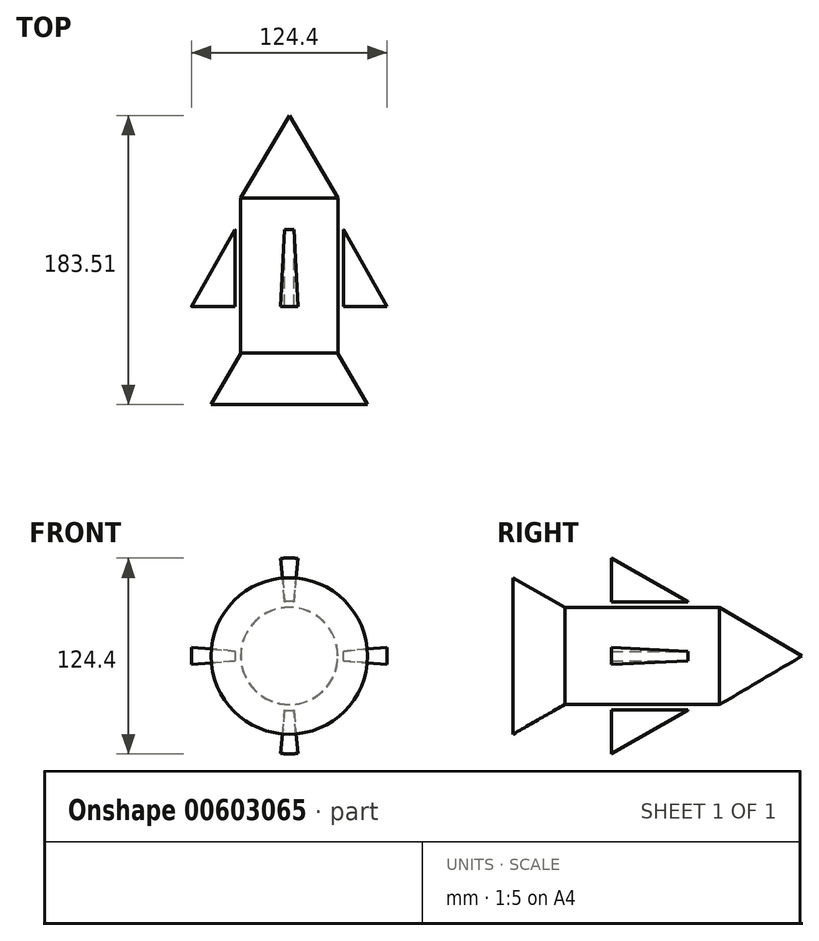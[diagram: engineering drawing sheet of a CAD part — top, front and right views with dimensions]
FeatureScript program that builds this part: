
annotation { "Feature Type Name" : "Feature", "Feature Type Description" : "" }
export const myFeature = defineFeature(function(context is Context, id is Id, definition is map)
    precondition{}
    {
        {
            var Q0;
            Q0=qCreatedBy(makeId("Front.planeOp"),FACE);
            var sketch = newSketch(context, id + "F0", { "sketchPlane" : qUnion([Q0])});
            skCircle(sketch, "E0", {"center": v(0, 0) * mm, "radius": 30.8 * mm});
            skSolve(sketch);
        }
        {
            var Q0;
            Q0 = qSketchRegion(id + "F0", true);
            extrude(context, id + "F1", {"entities" : qUnion([Q0]), "depth" : 98.3 * mm, "offsetDistance" : 25.4 * mm});
        }
        {
            var Q0;
            Q0=makeQuery(id+"F1.opExtrude","CAP_FACE",FACE,{"disambiguationData":[OSD([sQuery(id+"F0.wireOp",EDGE,"E0")])],"isStart":false});
            var sketch = newSketch(context, id + "F2", { "sketchPlane" : qUnion([Q0])});
            skCircle(sketch, "E1", {"center": v(0, 0) * mm, "radius": 30.77 * mm});
            skSolve(sketch);
        }
        {
            var Q0;
            Q0=makeQuery(id+"F2.imprint","IMPRINT",FACE,{"disambiguationData":[TD([[makeQuery(id+"F2.imprint","IMPRINT",EDGE,{"derivedFrom":sQuery(id+"F2.wireOp",EDGE,"E1")}),1.0]])]});
            extrude(context, id + "F3", {"entities" : qUnion([Q0]), "operationType" : NewBodyOperationType.ADD, "depth" : 32.77 * mm, "offsetDistance" : 25.4 * mm, "hasDraft" : true, "draftAngle" : 30 * degree});
        }
        {
            var Q0;
            Q0=qCreatedBy(makeId("Right.planeOp"),FACE);
            var sketch = newSketch(context, id + "F4", { "sketchPlane" : qUnion([Q0])});
            skLineSegment(sketch, "E2", {"start": v(0, 0) * mm, "end": v(52.45, 0) * mm});
            skLineSegment(sketch, "E3", {"start": v(52.45, 0) * mm, "end": v(0, 30.94) * mm});
            skLineSegment(sketch, "E4", {"start": v(0, 0) * mm, "end": v(0, 30.94) * mm});
            skSolve(sketch);
        }
        {
            var Q0;
            Q0=makeQuery(id+"F4.imprint","IMPRINT",FACE,{"disambiguationData":[TD([[makeQuery(id+"F4.imprint","IMPRINT",EDGE,{"derivedFrom":sQuery(id+"F4.wireOp",EDGE,"E2")}),1.0]])]});
            var Q1;
            Q1=sQuery(id+"F4.wireOp",EDGE,"E2");
            revolve(context, id + "F5", {"operationType" : NewBodyOperationType.ADD, "entities" : qUnion([Q0]), "axis" : qUnion([Q1]), "revolveType" : RevolveType.FULL});
        }
        {
            var Q0;
            Q0=qCreatedBy(makeId("Top.planeOp"),FACE);
            var sketch = newSketch(context, id + "F6", { "sketchPlane" : qUnion([Q0])});
            skLineSegment(sketch, "E5", {"start": v(0, -98.77) * mm, "end": v(0, 0) * mm});
            skSolve(sketch);
        }
        {
            var Q0;
            Q0=qCreatedBy(makeId("Top.planeOp"),FACE);
            var sketch = newSketch(context, id + "F7", { "sketchPlane" : qUnion([Q0])});
            skLineSegment(sketch, "E6", {"start": v(34.56, -68.74) * mm, "end": v(34.56, -20.03) * mm});
            skLineSegment(sketch, "E7", {"start": v(34.56, -68.74) * mm, "end": v(62.2, -68.74) * mm});
            skLineSegment(sketch, "E8", {"start": v(62.2, -68.74) * mm, "end": v(34.56, -20.03) * mm});
            skSolve(sketch);
        }
        {
            var Q0;
            Q0=makeQuery(id+"F7.imprint","IMPRINT",FACE,{"disambiguationData":[TD([[makeQuery(id+"F7.imprint","IMPRINT",EDGE,{"derivedFrom":sQuery(id+"F7.wireOp",EDGE,"E6")}),-1.0]])]});
            var Q1;
            Q1=makeQuery(id+"F1.opExtrude","SWEPT_FACE",FACE,{"disambiguationData":[OSD([sQuery(id+"F0.wireOp",EDGE,"E0")])]});
            revolve(context, id + "F8", {"entities" : qUnion([Q0]), "axis" : qUnion([Q1]), "revolveType" : RevolveType.TWO_DIRECTIONS, "angle" : 5 * degree, "angleBack" : 355 * degree});
        }
        {
            var Q0;
            Q0=makeQuery(id+"F8.opRevolve","SWEPT_BODY",BODY,{"disambiguationData":[OSD([sQuery(id+"F7.wireOp",EDGE,"E6"),sQuery(id+"F7.wireOp",EDGE,"E7"),sQuery(id+"F7.wireOp",EDGE,"E8")])]});
            var Q1;
            Q1=sQuery(id+"F6.wireOp",EDGE,"E5");
            circularPattern(context, id + "F9", {"entities" : qUnion([Q0]), "axis" : qUnion([Q1]), "angle" : 360 * degree, "instanceCount" : 4, "equalSpace" : true});
        }
    });
